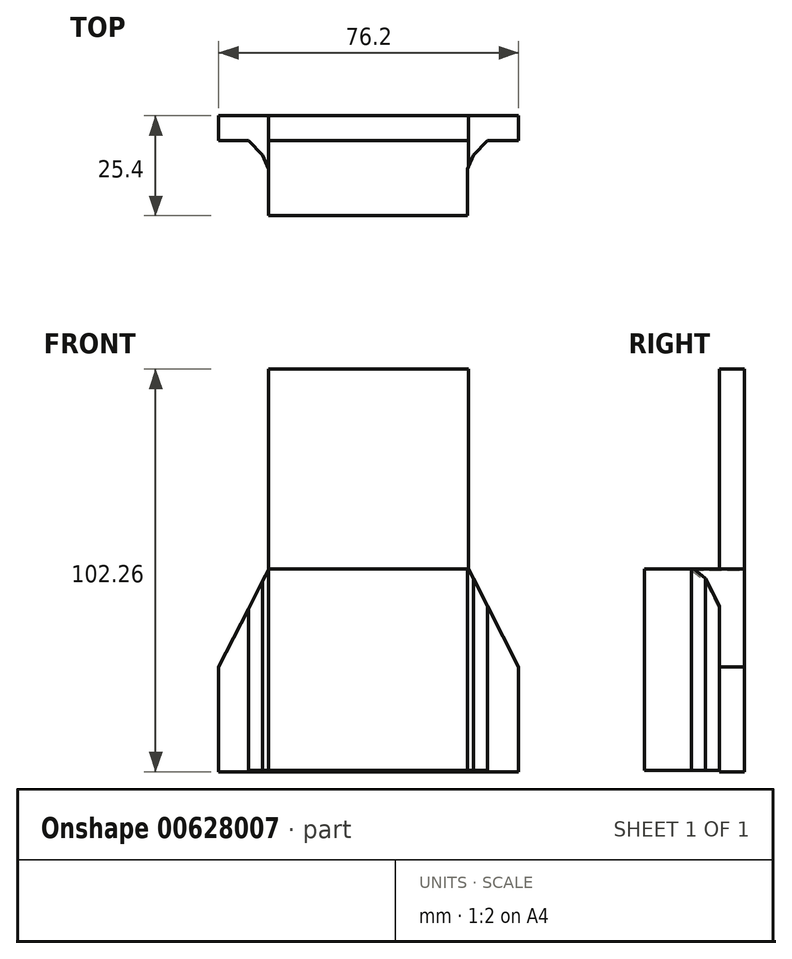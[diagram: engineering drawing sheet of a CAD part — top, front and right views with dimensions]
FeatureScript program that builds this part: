
annotation { "Feature Type Name" : "Feature", "Feature Type Description" : "" }
export const myFeature = defineFeature(function(context is Context, id is Id, definition is map)
    precondition{}
    {
        {
            var Q0;
            Q0=qCreatedBy(makeId("Front.planeOp"),FACE);
            var sketch = newSketch(context, id + "F0", { "sketchPlane" : qUnion([Q0])});
            skLineSegment(sketch, "E0.bottom", {"start": v(-25.4, -50.8) * mm, "end": v(25.4, -50.8) * mm});
            skLineSegment(sketch, "E0.top", {"start": v(-25.4, 50.8) * mm, "end": v(25.4, 50.8) * mm});
            skLineSegment(sketch, "E0.left", {"start": v(-25.4, -50.8) * mm, "end": v(-25.4, 50.8) * mm});
            skLineSegment(sketch, "E0.right", {"start": v(25.4, -50.8) * mm, "end": v(25.4, 50.8) * mm});
            skPoint(sketch, "E0.middle", {"position": v(0, 0) * mm});
            skLineSegment(sketch, "E1.bottom", {"start": v(-38.1, -51.46) * mm, "end": v(38.1, -51.46) * mm});
            skLineSegment(sketch, "E1.top", {"start": v(-38.1, -24.79) * mm, "end": v(38.1, -24.79) * mm});
            skLineSegment(sketch, "E1.left", {"start": v(-38.1, -51.46) * mm, "end": v(-38.1, -24.79) * mm});
            skLineSegment(sketch, "E1.right", {"start": v(38.1, -51.46) * mm, "end": v(38.1, -24.79) * mm});
            skPoint(sketch, "E1.middle", {"position": v(0, -38.12) * mm});
            skLineSegment(sketch, "E2", {"start": v(-38.1, -24.79) * mm, "end": v(-25.4, 0) * mm});
            skLineSegment(sketch, "E3", {"start": v(-25.4, 0) * mm, "end": v(-25.4, -24.79) * mm});
            skLineSegment(sketch, "E4", {"start": v(-25.4, -24.79) * mm, "end": v(-38.1, -24.79) * mm});
            skLineSegment(sketch, "E5", {"start": v(-25.4, -24.79) * mm, "end": v(-25.4, -50.8) * mm});
            skLineSegment(sketch, "E6", {"start": v(38.1, -24.79) * mm, "end": v(25.4, 0) * mm});
            skLineSegment(sketch, "E7", {"start": v(25.4, 0) * mm, "end": v(25.4, -24.79) * mm});
            skLineSegment(sketch, "E8", {"start": v(25.4, -24.79) * mm, "end": v(38.1, -24.79) * mm});
            skSolve(sketch);
        }
        {
            var Q0;
            {var subQ0=sQuery(id+"F0.wireOp",EDGE,"E0.bottom");Q0=makeQuery(id+"F0.imprint","IMPRINT",FACE,{"disambiguationData":[TD([[makeQuery(id+"F0.imprint","IMPRINT",EDGE,{"derivedFrom":subQ0}),1.0]])]});}
            var Q1;
            Q1=makeQuery(id+"F0.imprint","IMPRINT",FACE,{"disambiguationData":[TD([[makeQuery(id+"F0.imprint","IMPRINT",EDGE,{"derivedFrom":sQuery(id+"F0.wireOp",EDGE,"E2")}),-1.0]])]});
            var Q2;
            {var subQ1=sQuery(id+"F0.wireOp",EDGE,"E0.bottom");Q2=makeQuery(id+"F0.imprint","IMPRINT",FACE,{"disambiguationData":[TD([[makeQuery(id+"F0.imprint","IMPRINT",EDGE,{"derivedFrom":subQ1}),-1.0]])]});}
            var Q3;
            Q3=makeQuery(id+"F0.imprint","IMPRINT",FACE,{"disambiguationData":[TD([[makeQuery(id+"F0.imprint","IMPRINT",EDGE,{"derivedFrom":sQuery(id+"F0.wireOp",EDGE,"E6")}),1.0]])]});
            var Q4;
            {var subQ1=sQuery(id+"F0.wireOp",EDGE,"E0.top");Q4=makeQuery(id+"F0.imprint","IMPRINT",FACE,{"disambiguationData":[TD([[makeQuery(id+"F0.imprint","IMPRINT",EDGE,{"derivedFrom":subQ1}),-1.0]])]});}
            extrude(context, id + "F1", {"entities" : qUnion([Q0, Q1, Q2, Q3, Q4]), "depth" : 6.35 * mm, "offsetDistance" : 25.4 * mm});
        }
        {
            var Q0;
            Q0=qCreatedBy(makeId("Front.planeOp"),FACE);
            var sketch = newSketch(context, id + "F2", { "sketchPlane" : qUnion([Q0])});
            skLineSegment(sketch, "E9.bottom", {"start": v(-25.47, 0) * mm, "end": v(25.13, 0) * mm});
            skLineSegment(sketch, "E9.top", {"start": v(-25.47, -51.12) * mm, "end": v(25.13, -51.12) * mm});
            skLineSegment(sketch, "E9.left", {"start": v(-25.47, 0) * mm, "end": v(-25.47, -51.12) * mm});
            skLineSegment(sketch, "E9.right", {"start": v(25.13, 0) * mm, "end": v(25.13, -51.12) * mm});
            skSolve(sketch);
        }
        {
            var Q0;
            Q0 = qSketchRegion(id + "F2", true);
            extrude(context, id + "F3", {"entities" : qUnion([Q0]), "operationType" : NewBodyOperationType.ADD, "depth" : 25.4 * mm, "offsetDistance" : 25.4 * mm});
        }
        {
            var Q0;
            Q0=makeQuery(id+"F3.boolean.opBoolean","INTERSECT",EDGE,{"derivedFrom":[makeQuery(id+"F1.opExtrude","CAP_FACE",FACE,{"disambiguationData":[OSD([sQuery(id+"F0.wireOp",EDGE,"E0.top"),sQuery(id+"F0.wireOp",EDGE,"E0.left"),sQuery(id+"F0.wireOp",EDGE,"E0.right"),sQuery(id+"F0.wireOp",EDGE,"E1.bottom"),sQuery(id+"F0.wireOp",EDGE,"E1.right"),sQuery(id+"F0.wireOp",EDGE,"E2"),sQuery(id+"F0.wireOp",EDGE,"E1.left"),sQuery(id+"F0.wireOp",EDGE,"E6")])],"isStart":false}),makeQuery(id+"F3.opExtrude","SWEPT_FACE",FACE,{"disambiguationData":[OSD([sQuery(id+"F2.wireOp",EDGE,"E9.right")])]})]});
            var Q1;
            Q1=makeQuery(id+"F3.boolean.opBoolean","INTERSECT",EDGE,{"derivedFrom":[makeQuery(id+"F1.opExtrude","CAP_FACE",FACE,{"disambiguationData":[OSD([sQuery(id+"F0.wireOp",EDGE,"E0.top"),sQuery(id+"F0.wireOp",EDGE,"E0.left"),sQuery(id+"F0.wireOp",EDGE,"E0.right"),sQuery(id+"F0.wireOp",EDGE,"E1.bottom"),sQuery(id+"F0.wireOp",EDGE,"E1.right"),sQuery(id+"F0.wireOp",EDGE,"E2"),sQuery(id+"F0.wireOp",EDGE,"E1.left"),sQuery(id+"F0.wireOp",EDGE,"E6")])],"isStart":false}),makeQuery(id+"F3.opExtrude","SWEPT_FACE",FACE,{"disambiguationData":[OSD([sQuery(id+"F2.wireOp",EDGE,"E9.left")])]})]});
            chamfer(context, id + "F4", {"entities" : qUnion([Q0, Q1]), "width" : 5.08 * mm, "tangentPropagation" : true});
        }
        {
            var Q0;
            {var subQ0=makeQuery(id+"F3.opExtrude","SWEPT_FACE",FACE,{"disambiguationData":[OSD([sQuery(id+"F2.wireOp",EDGE,"E9.right")])]});Q0=makeQuery(id+"F4.opChamfer","BLEND_EDGE",EDGE,{"blendedFrom":[makeQuery(id+"F3.boolean.opBoolean","INTERSECT",EDGE,{"derivedFrom":[makeQuery(id+"F1.opExtrude","CAP_FACE",FACE,{"disambiguationData":[OSD([sQuery(id+"F0.wireOp",EDGE,"E0.top"),sQuery(id+"F0.wireOp",EDGE,"E0.left"),sQuery(id+"F0.wireOp",EDGE,"E0.right"),sQuery(id+"F0.wireOp",EDGE,"E1.bottom"),sQuery(id+"F0.wireOp",EDGE,"E1.right"),sQuery(id+"F0.wireOp",EDGE,"E2"),sQuery(id+"F0.wireOp",EDGE,"E1.left"),sQuery(id+"F0.wireOp",EDGE,"E6")])],"isStart":false}),subQ0]}),subQ0],"blendedInto":[subQ0]});}
            var Q1;
            {var subQ0=makeQuery(id+"F3.opExtrude","SWEPT_FACE",FACE,{"disambiguationData":[OSD([sQuery(id+"F2.wireOp",EDGE,"E9.left")])]});Q1=makeQuery(id+"F4.opChamfer","BLEND_EDGE",EDGE,{"blendedFrom":[makeQuery(id+"F3.boolean.opBoolean","INTERSECT",EDGE,{"derivedFrom":[makeQuery(id+"F1.opExtrude","CAP_FACE",FACE,{"disambiguationData":[OSD([sQuery(id+"F0.wireOp",EDGE,"E0.top"),sQuery(id+"F0.wireOp",EDGE,"E0.left"),sQuery(id+"F0.wireOp",EDGE,"E0.right"),sQuery(id+"F0.wireOp",EDGE,"E1.bottom"),sQuery(id+"F0.wireOp",EDGE,"E1.right"),sQuery(id+"F0.wireOp",EDGE,"E2"),sQuery(id+"F0.wireOp",EDGE,"E1.left"),sQuery(id+"F0.wireOp",EDGE,"E6")])],"isStart":false}),subQ0]}),subQ0],"blendedInto":[subQ0]});}
            chamfer(context, id + "F5", {"entities" : qUnion([Q0, Q1]), "width" : 5.08 * mm, "tangentPropagation" : true});
        }
    });
